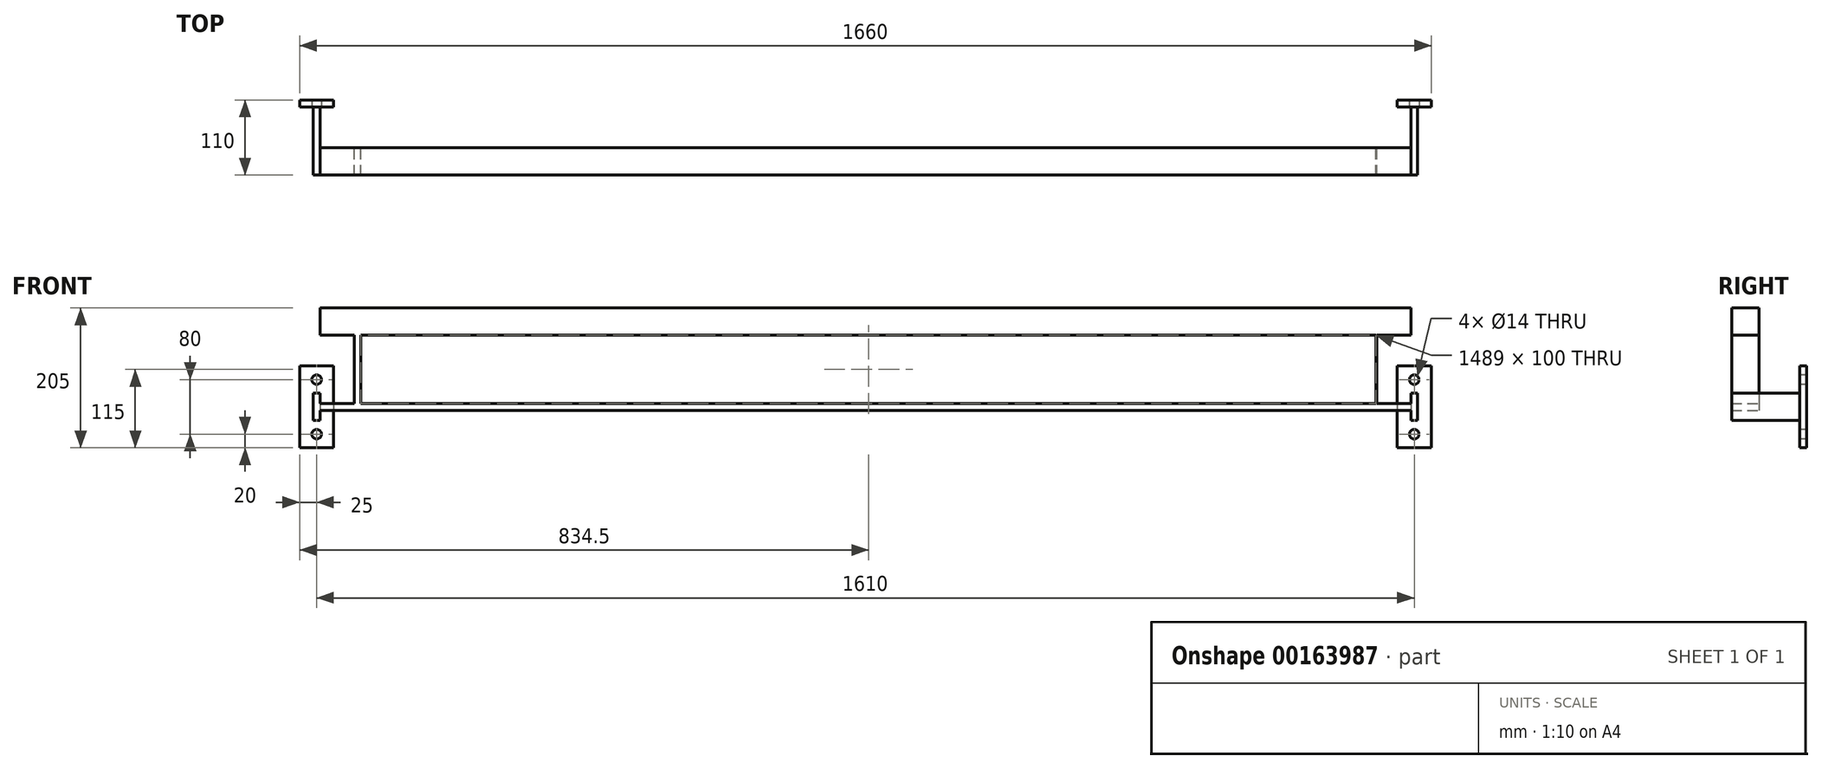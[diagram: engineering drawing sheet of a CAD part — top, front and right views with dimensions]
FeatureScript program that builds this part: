
annotation { "Feature Type Name" : "Feature", "Feature Type Description" : "" }
export const myFeature = defineFeature(function(context is Context, id is Id, definition is map)
    precondition{}
    {
        {
            var Q0;
            Q0=qCreatedBy(makeId("Right.planeOp"),FACE);
            var sketch = newSketch(context, id + "F0", { "sketchPlane" : qUnion([Q0])});
            skLineSegment(sketch, "E0.bottom", {"start": v(-20, -20) * mm, "end": v(20, -20) * mm});
            skLineSegment(sketch, "E0.top", {"start": v(-20, 20) * mm, "end": v(20, 20) * mm});
            skLineSegment(sketch, "E0.left", {"start": v(-20, -20) * mm, "end": v(-20, 20) * mm});
            skLineSegment(sketch, "E0.right", {"start": v(20, -20) * mm, "end": v(20, 20) * mm});
            skPoint(sketch, "E0.middle", {"position": v(0, 0) * mm});
            skSolve(sketch);
        }
        {
            var Q0;
            Q0 = qSketchRegion(id + "F0", true);
            extrude(context, id + "F1", {"entities" : qUnion([Q0]), "depth" : 800 * mm, "hasSecondDirection" : true, "secondDirectionOppositeDirection" : true, "secondDirectionDepth" : 800 * mm});
        }
        {
            var Q0;
            Q0=qCreatedBy(makeId("Right.planeOp"),FACE);
            cPlane(context, id + "F2", {"entities" : qUnion([Q0]), "cplaneType" : CPlaneType.OFFSET, "offset" : 750 * mm, "width" : 150 * mm, "height" : 150 * mm});
        }
        {
            var Q0;
            Q0=qCreatedBy(makeId("Right.planeOp"),FACE);
            cPlane(context, id + "F3", {"entities" : qUnion([Q0]), "cplaneType" : CPlaneType.OFFSET, "offset" : 750 * mm, "oppositeDirection" : true, "width" : 150 * mm, "height" : 150 * mm});
        }
        {
            var Q0;
            Q0=qCreatedBy(id+"F3.planeOp",FACE);
            var sketch = newSketch(context, id + "F4", { "sketchPlane" : qUnion([Q0])});
            skLineSegment(sketch, "E1.bottom", {"start": v(-20, -20) * mm, "end": v(20, -20) * mm});
            skLineSegment(sketch, "E1.top", {"start": v(-20, -120) * mm, "end": v(20, -120) * mm});
            skLineSegment(sketch, "E1.left", {"start": v(-20, -20) * mm, "end": v(-20, -120) * mm});
            skLineSegment(sketch, "E1.right", {"start": v(20, -20) * mm, "end": v(20, -120) * mm});
            skSolve(sketch);
        }
        {
            var Q0;
            Q0 = qSketchRegion(id + "F4", true);
            extrude(context, id + "F5", {"entities" : qUnion([Q0]), "operationType" : NewBodyOperationType.ADD, "depth" : 10 * mm});
        }
        {
            var Q0;
            Q0=qCreatedBy(id+"F2.planeOp",FACE);
            var sketch = newSketch(context, id + "F6", { "sketchPlane" : qUnion([Q0])});
            skLineSegment(sketch, "E2.bottom", {"start": v(-20, -20) * mm, "end": v(20, -20) * mm});
            skLineSegment(sketch, "E2.top", {"start": v(-20, -120) * mm, "end": v(20, -120) * mm});
            skLineSegment(sketch, "E2.left", {"start": v(-20, -20) * mm, "end": v(-20, -120) * mm});
            skLineSegment(sketch, "E2.right", {"start": v(20, -20) * mm, "end": v(20, -120) * mm});
            skSolve(sketch);
        }
        {
            var Q0;
            Q0 = qSketchRegion(id + "F6", true);
            extrude(context, id + "F7", {"entities" : qUnion([Q0]), "operationType" : NewBodyOperationType.ADD, "oppositeDirection" : true, "depth" : 1 * mm});
        }
        {
            var Q0;
            Q0=qCreatedBy(makeId("Right.planeOp"),FACE);
            var sketch = newSketch(context, id + "F8", { "sketchPlane" : qUnion([Q0])});
            skLineSegment(sketch, "E3.bottom", {"start": v(-20, -120) * mm, "end": v(20, -120) * mm});
            skLineSegment(sketch, "E3.top", {"start": v(-20, -130) * mm, "end": v(20, -130) * mm});
            skLineSegment(sketch, "E3.left", {"start": v(-20, -120) * mm, "end": v(-20, -130) * mm});
            skLineSegment(sketch, "E3.right", {"start": v(20, -120) * mm, "end": v(20, -130) * mm});
            skSolve(sketch);
        }
        {
            var Q0;
            Q0 = qSketchRegion(id + "F8", true);
            extrude(context, id + "F9", {"entities" : qUnion([Q0]), "operationType" : NewBodyOperationType.ADD, "depth" : 800 * mm, "hasSecondDirection" : true, "secondDirectionOppositeDirection" : true, "secondDirectionDepth" : 800 * mm});
        }
        {
            var Q0;
            Q0=makeQuery(id+"F9.opExtrude","CAP_FACE",FACE,{"disambiguationData":[OSD([sQuery(id+"F8.wireOp",EDGE,"E3.bottom"),sQuery(id+"F8.wireOp",EDGE,"E3.top"),sQuery(id+"F8.wireOp",EDGE,"E3.left"),sQuery(id+"F8.wireOp",EDGE,"E3.right")])],"isStart":false});
            var sketch = newSketch(context, id + "F10", { "sketchPlane" : qUnion([Q0])});
            skLineSegment(sketch, "E4.bottom", {"start": v(-20, -105) * mm, "end": v(80, -105) * mm});
            skLineSegment(sketch, "E4.top", {"start": v(-20, -145) * mm, "end": v(80, -145) * mm});
            skLineSegment(sketch, "E4.left", {"start": v(-20, -105) * mm, "end": v(-20, -145) * mm});
            skLineSegment(sketch, "E4.right", {"start": v(80, -105) * mm, "end": v(80, -145) * mm});
            skSolve(sketch);
        }
        {
            var Q0;
            Q0 = qSketchRegion(id + "F10", true);
            extrude(context, id + "F11", {"entities" : qUnion([Q0]), "operationType" : NewBodyOperationType.ADD, "depth" : 10 * mm});
        }
        {
            var Q0;
            Q0=makeQuery(id+"F9.opExtrude","CAP_FACE",FACE,{"disambiguationData":[OSD([sQuery(id+"F8.wireOp",EDGE,"E3.bottom"),sQuery(id+"F8.wireOp",EDGE,"E3.top"),sQuery(id+"F8.wireOp",EDGE,"E3.left"),sQuery(id+"F8.wireOp",EDGE,"E3.right")])],"isStart":true});
            var sketch = newSketch(context, id + "F12", { "sketchPlane" : qUnion([Q0])});
            skLineSegment(sketch, "E5.bottom", {"start": v(-80, -105) * mm, "end": v(20, -105) * mm});
            skLineSegment(sketch, "E5.top", {"start": v(-80, -145) * mm, "end": v(20, -145) * mm});
            skLineSegment(sketch, "E5.left", {"start": v(-80, -105) * mm, "end": v(-80, -145) * mm});
            skLineSegment(sketch, "E5.right", {"start": v(20, -105) * mm, "end": v(20, -145) * mm});
            skSolve(sketch);
        }
        {
            var Q0;
            Q0 = qSketchRegion(id + "F12", true);
            extrude(context, id + "F13", {"entities" : qUnion([Q0]), "operationType" : NewBodyOperationType.ADD, "depth" : 10 * mm});
        }
        {
            var Q0;
            Q0=makeQuery(id+"F11.opExtrude","SWEPT_FACE",FACE,{"disambiguationData":[OSD([sQuery(id+"F10.wireOp",EDGE,"E4.right")])]});
            var sketch = newSketch(context, id + "F14", { "sketchPlane" : qUnion([Q0])});
            skLineSegment(sketch, "E6.bottom", {"start": v(-830, -65) * mm, "end": v(-780, -65) * mm});
            skLineSegment(sketch, "E6.top", {"start": v(-830, -185) * mm, "end": v(-780, -185) * mm});
            skLineSegment(sketch, "E6.left", {"start": v(-830, -65) * mm, "end": v(-830, -185) * mm});
            skLineSegment(sketch, "E6.right", {"start": v(-780, -65) * mm, "end": v(-780, -185) * mm});
            skCircle(sketch, "E7", {"center": v(-805, -85) * mm, "radius": 7 * mm});
            skPoint(sketch, "E7.centerSnap0", {"position": v(-805, -65) * mm});
            skCircle(sketch, "E8", {"center": v(-805, -165) * mm, "radius": 7 * mm});
            skPoint(sketch, "E8.centerSnap0", {"position": v(-805, -185) * mm});
            skSolve(sketch);
        }
        {
            var Q0;
            Q0 = qSketchRegion(id + "F14", true);
            extrude(context, id + "F15", {"entities" : qUnion([Q0]), "operationType" : NewBodyOperationType.ADD, "depth" : 10 * mm});
        }
        {
            var Q0;
            Q0=makeQuery(id+"F13.opExtrude","SWEPT_FACE",FACE,{"disambiguationData":[OSD([sQuery(id+"F12.wireOp",EDGE,"E5.left")])]});
            var sketch = newSketch(context, id + "F16", { "sketchPlane" : qUnion([Q0])});
            skLineSegment(sketch, "E9.bottom", {"start": v(780, -65) * mm, "end": v(830, -65) * mm});
            skLineSegment(sketch, "E9.top", {"start": v(780, -185) * mm, "end": v(830, -185) * mm});
            skLineSegment(sketch, "E9.left", {"start": v(780, -65) * mm, "end": v(780, -185) * mm});
            skLineSegment(sketch, "E9.right", {"start": v(830, -65) * mm, "end": v(830, -185) * mm});
            skCircle(sketch, "E10", {"center": v(805, -165) * mm, "radius": 7 * mm});
            skPoint(sketch, "E10.centerSnap0", {"position": v(805, -185) * mm});
            skCircle(sketch, "E11", {"center": v(805, -85) * mm, "radius": 7 * mm});
            skPoint(sketch, "E11.centerSnap0", {"position": v(805, -65) * mm});
            skSolve(sketch);
        }
        {
            var Q0;
            Q0 = qSketchRegion(id + "F16", true);
            extrude(context, id + "F17", {"entities" : qUnion([Q0]), "operationType" : NewBodyOperationType.ADD, "depth" : 10 * mm});
        }
    });
